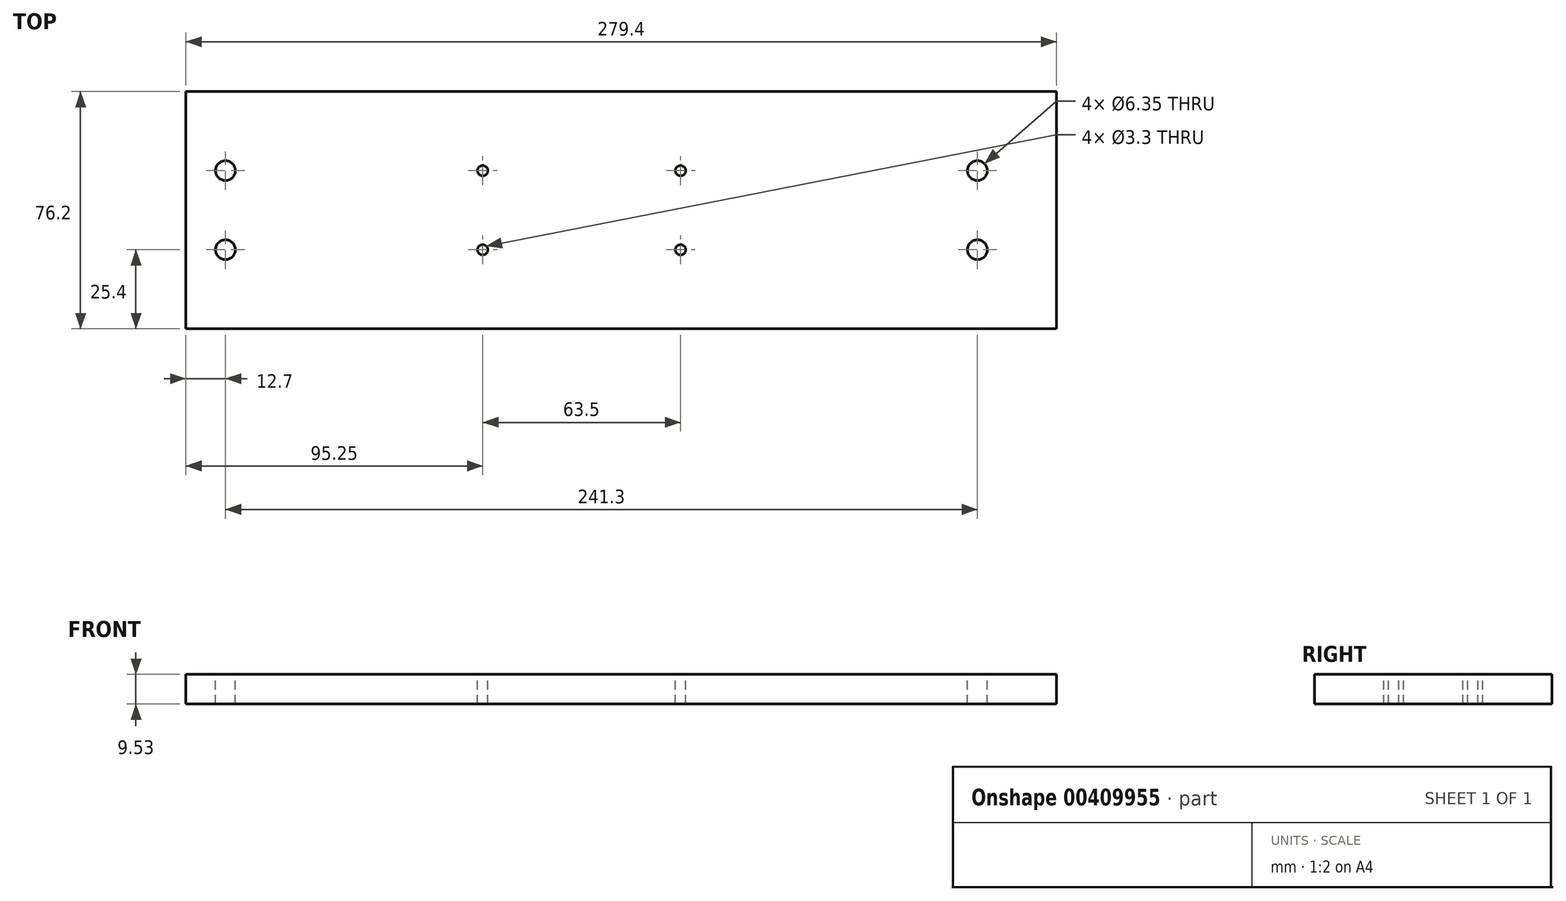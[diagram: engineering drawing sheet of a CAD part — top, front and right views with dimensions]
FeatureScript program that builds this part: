
annotation { "Feature Type Name" : "Feature", "Feature Type Description" : "" }
export const myFeature = defineFeature(function(context is Context, id is Id, definition is map)
    precondition{}
    {
        {
            var Q0;
            Q0=qCreatedBy(makeId("Top.planeOp"),FACE);
            var sketch = newSketch(context, id + "F0", { "sketchPlane" : qUnion([Q0])});
            skLineSegment(sketch, "E0.bottom", {"start": v(-139.7, 38.1) * mm, "end": v(139.7, 38.1) * mm});
            skLineSegment(sketch, "E0.top", {"start": v(-139.7, -38.1) * mm, "end": v(139.7, -38.1) * mm});
            skLineSegment(sketch, "E0.left", {"start": v(-139.7, 38.1) * mm, "end": v(-139.7, -38.1) * mm});
            skLineSegment(sketch, "E0.right", {"start": v(139.7, 38.1) * mm, "end": v(139.7, -38.1) * mm});
            skLineSegment(sketch, "E1", {"start": v(-113.57, 0) * mm, "end": v(160.82, 0) * mm, "construction": true});
            skSolve(sketch);
        }
        {
            var Q0;
            Q0 = qSketchRegion(id + "F0", true);
            extrude(context, id + "F1", {"entities" : qUnion([Q0]), "depth" : 9.52 * mm});
        }
        {
            var Q0;
            Q0=makeQuery(id+"F1.opExtrude","CAP_FACE",FACE,{"disambiguationData":[OSD([sQuery(id+"F0.wireOp",EDGE,"E0.bottom"),sQuery(id+"F0.wireOp",EDGE,"E0.top"),sQuery(id+"F0.wireOp",EDGE,"E0.left"),sQuery(id+"F0.wireOp",EDGE,"E0.right")])],"isStart":false});
            var sketch = newSketch(context, id + "F2", { "sketchPlane" : qUnion([Q0])});
            skLineSegment(sketch, "E2", {"start": v(-168.91, 0) * mm, "end": v(166.69, 0) * mm, "construction": true});
            skCircle(sketch, "E3", {"center": v(-127, 12.7) * mm, "radius": 3.17 * mm});
            skCircle(sketch, "E4.MirrorC", {"center": v(-127, -12.7) * mm, "radius": 3.17 * mm});
            skCircle(sketch, "E5", {"center": v(-44.45, 12.7) * mm, "radius": 1.65 * mm});
            skCircle(sketch, "E6.MirrorC", {"center": v(-44.45, -12.7) * mm, "radius": 1.65 * mm});
            skCircle(sketch, "E7.1.0.0", {"center": v(19.05, 12.7) * mm, "radius": 1.65 * mm});
            skCircle(sketch, "E7.1.0.1", {"center": v(19.05, -12.7) * mm, "radius": 1.65 * mm});
            skLineSegment(sketch, "E7.direction1", {"start": v(-44.45, 12.7) * mm, "end": v(19.05, 12.7) * mm, "construction": true});
            skCircle(sketch, "E8", {"center": v(114.3, 12.7) * mm, "radius": 3.18 * mm});
            skCircle(sketch, "E9.MirrorC", {"center": v(114.3, -12.7) * mm, "radius": 3.18 * mm});
            skSolve(sketch);
        }
        {
            var Q0;
            Q0 = qSketchRegion(id + "F2", true);
            extrude(context, id + "F3", {"entities" : qUnion([Q0]), "operationType" : NewBodyOperationType.REMOVE, "endBound" : BoundingType.THROUGH_ALL, "oppositeDirection" : true, "depth" : 25.4 * mm});
        }
    });
